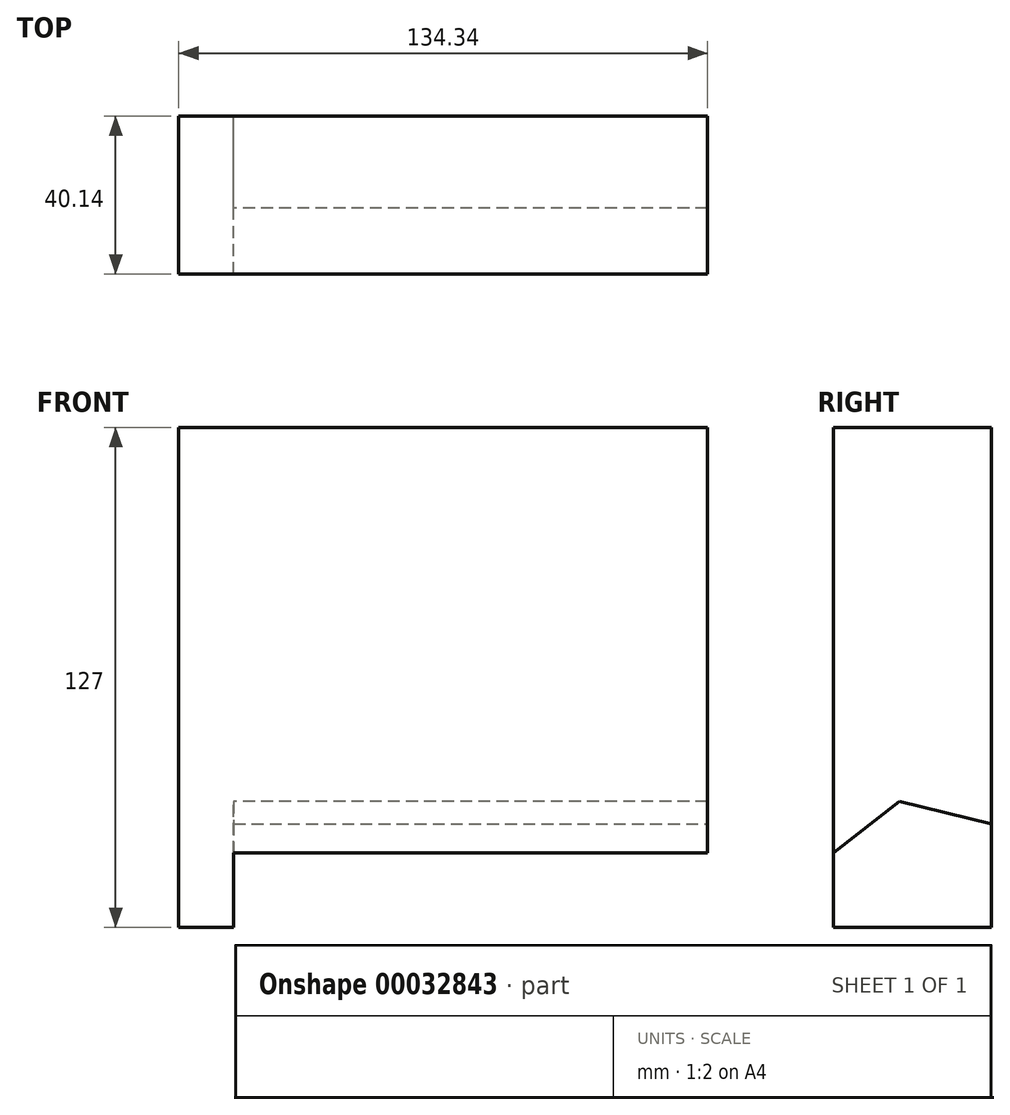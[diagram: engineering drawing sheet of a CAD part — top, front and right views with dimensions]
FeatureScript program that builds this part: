
annotation { "Feature Type Name" : "Feature", "Feature Type Description" : "" }
export const myFeature = defineFeature(function(context is Context, id is Id, definition is map)
    precondition{}
    {
        {
            var Q0;
            Q0=qCreatedBy(makeId("Top.planeOp"),FACE);
            var sketch = newSketch(context, id + "F0", { "sketchPlane" : qUnion([Q0])});
            skLineSegment(sketch, "E0.bottom", {"start": v(-13.95, -23.66) * mm, "end": v(120.4, -23.66) * mm});
            skLineSegment(sketch, "E0.top", {"start": v(-13.95, 16.48) * mm, "end": v(120.4, 16.48) * mm});
            skLineSegment(sketch, "E0.left", {"start": v(-13.95, -23.66) * mm, "end": v(-13.95, 16.48) * mm});
            skLineSegment(sketch, "E0.right", {"start": v(120.4, -23.66) * mm, "end": v(120.4, 16.48) * mm});
            skSolve(sketch);
        }
        {
            var Q0;
            Q0=makeQuery(id+"F0.imprint","IMPRINT",FACE,{"disambiguationData":[TD([[makeQuery(id+"F0.imprint","IMPRINT",EDGE,{"derivedFrom":sQuery(id+"F0.wireOp",EDGE,"E0.bottom")}),1.0]])]});
            extrude(context, id + "F1", {"entities" : qUnion([Q0]), "depth" : 127 * mm});
        }
        {
            var Q0;
            Q0=qCreatedBy(makeId("Right.planeOp"),FACE);
            var sketch = newSketch(context, id + "F2", { "sketchPlane" : qUnion([Q0])});
            skCircle(sketch, "E1.cCircle", {"center": v(0, 0) * mm, "radius": 29.47 * mm, "construction": true});
            skLineSegment(sketch, "E1.0", {"start": v(32.7, -0.4) * mm, "end": v(20.08, -25.82) * mm});
            skLineSegment(sketch, "E1.1", {"start": v(20.08, -25.82) * mm, "end": v(-7.67, -31.8) * mm});
            skLineSegment(sketch, "E1.2", {"start": v(-7.67, -31.8) * mm, "end": v(-29.64, -13.83) * mm});
            skLineSegment(sketch, "E1.3", {"start": v(-29.64, -13.83) * mm, "end": v(-29.3, 14.55) * mm});
            skLineSegment(sketch, "E1.4", {"start": v(-29.3, 14.55) * mm, "end": v(-6.89, 31.98) * mm});
            skLineSegment(sketch, "E1.5", {"start": v(-6.89, 31.98) * mm, "end": v(20.7, 25.32) * mm});
            skLineSegment(sketch, "E1.6", {"start": v(20.7, 25.32) * mm, "end": v(32.7, -0.4) * mm});
            skPoint(sketch, "E1.0.midPoint", {"position": v(26.4, -13.11) * mm});
            skSolve(sketch);
        }
        {
            var Q0;
            Q0=makeQuery(id+"F2.imprint","IMPRINT",FACE,{"disambiguationData":[TD([[makeQuery(id+"F2.imprint","IMPRINT",EDGE,{"derivedFrom":sQuery(id+"F2.wireOp",EDGE,"E1.0")}),-1.0]])]});
            extrude(context, id + "F3", {"entities" : qUnion([Q0]), "operationType" : NewBodyOperationType.REMOVE, "endBound" : BoundingType.THROUGH_ALL, "depth" : 25.4 * mm});
        }
    });
